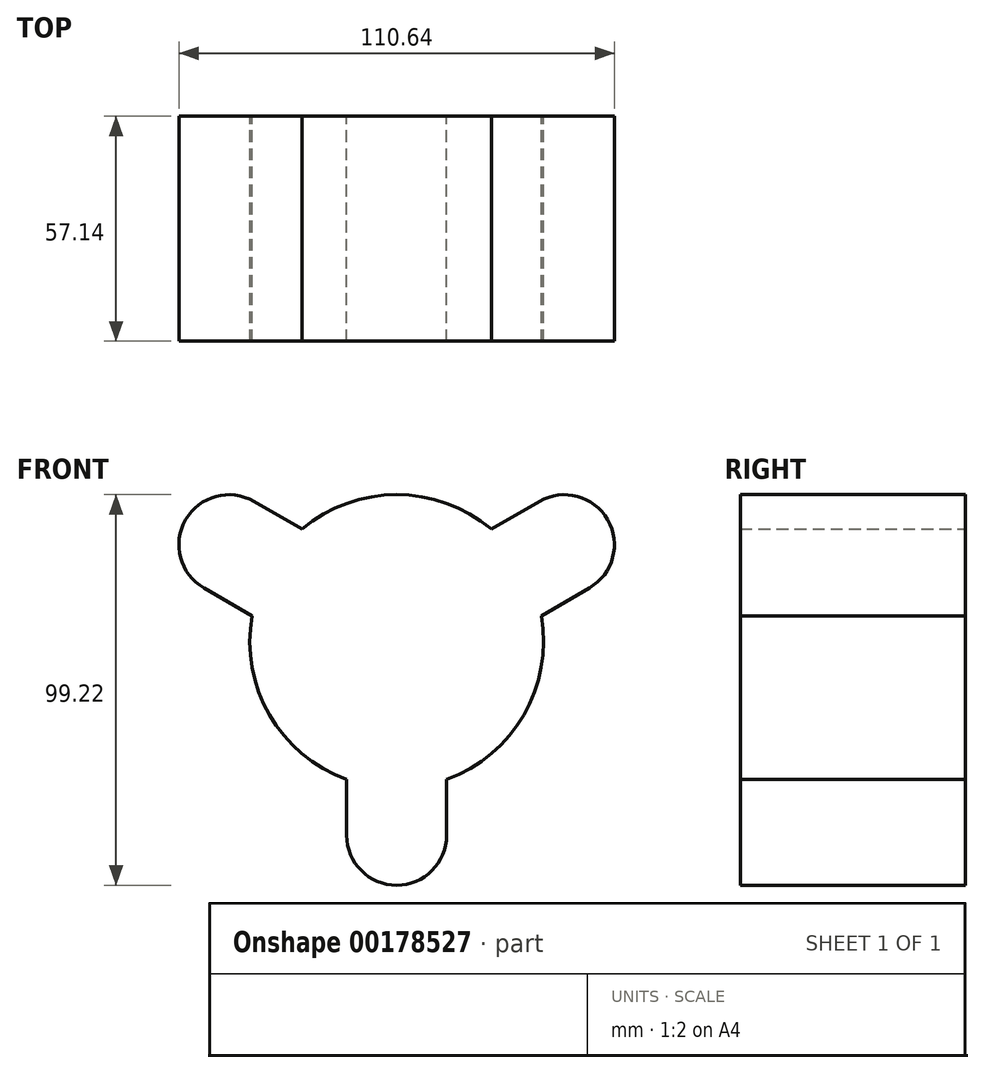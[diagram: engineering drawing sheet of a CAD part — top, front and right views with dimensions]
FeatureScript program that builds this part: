
annotation { "Feature Type Name" : "Feature", "Feature Type Description" : "" }
export const myFeature = defineFeature(function(context is Context, id is Id, definition is map)
    precondition{}
    {
        {
            var Q0;
            Q0=qCreatedBy(makeId("Front.planeOp"),FACE);
            var sketch = newSketch(context, id + "F0", { "sketchPlane" : qUnion([Q0])});
            skArc(sketch, "E0", {"start": v(12.7, -35.08) * mm, "mid": v(32.3, -18.65) * mm, "end": v(36.73, 6.54) * mm});
            skLineSegment(sketch, "E1", {"start": v(-37.3, 0) * mm, "end": v(37.3, 0) * mm, "construction": true});
            skLineSegment(sketch, "E2", {"start": v(0, 37.3) * mm, "end": v(0, -37.3) * mm, "construction": true});
            skPoint(sketch, "E3", {"position": v(0, -49.21) * mm});
            skArc(sketch, "E4", {"start": v(-12.7, -49.21) * mm, "mid": v(0, -61.91) * mm, "end": v(12.7, -49.21) * mm});
            skLineSegment(sketch, "E5", {"start": v(-12.7, -49.21) * mm, "end": v(-12.7, -35.08) * mm});
            skLineSegment(sketch, "E6", {"start": v(12.7, -49.21) * mm, "end": v(12.7, -35.08) * mm});
            skLineSegment(sketch, "E7.1.0", {"start": v(36.27, 35.6) * mm, "end": v(24.03, 28.54) * mm});
            skLineSegment(sketch, "E7.1.1", {"start": v(48.97, 13.6) * mm, "end": v(36.73, 6.54) * mm});
            skArc(sketch, "E7.1.2", {"start": v(48.97, 13.6) * mm, "mid": v(53.62, 30.96) * mm, "end": v(36.27, 35.6) * mm});
            skPoint(sketch, "E7.1.3", {"position": v(42.62, 24.6) * mm});
            skLineSegment(sketch, "E7.2.0", {"start": v(-48.97, 13.6) * mm, "end": v(-36.73, 6.54) * mm});
            skLineSegment(sketch, "E7.2.1", {"start": v(-36.27, 35.6) * mm, "end": v(-24.03, 28.54) * mm});
            skArc(sketch, "E7.2.2", {"start": v(-36.27, 35.6) * mm, "mid": v(-53.62, 30.96) * mm, "end": v(-48.97, 13.6) * mm});
            skPoint(sketch, "E7.2.3", {"position": v(-42.62, 24.6) * mm});
            skArc(sketch, "E8.trimOffspring", {"start": v(-36.73, 6.54) * mm, "mid": v(-32.3, -18.65) * mm, "end": v(-12.7, -35.08) * mm});
            skArc(sketch, "E9.trimOffspring", {"start": v(24.03, 28.54) * mm, "mid": v(0, 37.3) * mm, "end": v(-24.03, 28.54) * mm});
            skSolve(sketch);
        }
        {
            var Q0;
            Q0 = qSketchRegion(id + "F0", true);
            extrude(context, id + "F1", {"entities" : qUnion([Q0]), "depth" : 28.57 * mm, "hasSecondDirection" : true, "secondDirectionOppositeDirection" : true, "secondDirectionDepth" : 28.57 * mm});
        }
    });
